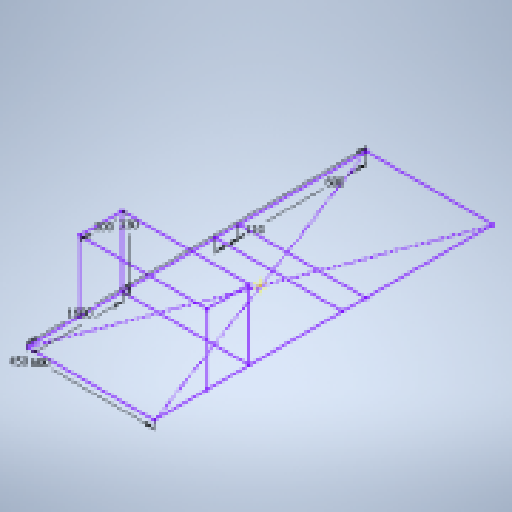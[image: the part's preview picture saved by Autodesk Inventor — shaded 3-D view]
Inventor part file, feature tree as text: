
AUTODESK INVENTOR PART (.ipt)
format: ipt  version: 2025.1 (Build 291241020, 241B)  size: 141,824 bytes
history: native  units: in
note: dims shown in document units (in); Inventor stores cm internally (conversion verified against a paired STEP export)
features: sketch x2
ambient origin geometry x8: Origin, YZ Plane, XZ Plane, XY Plane, X Axis, Y Axis, Z Axis, Center Point
feature tree (2):
  sketch  "Sketch3"  dims[d4=62.9921in d5=23.622in d7=23.622in d8=4.3307in d9=17.7165in d10=12.9921in d11=7.874in]
  sketch  "3D Sketch3"
